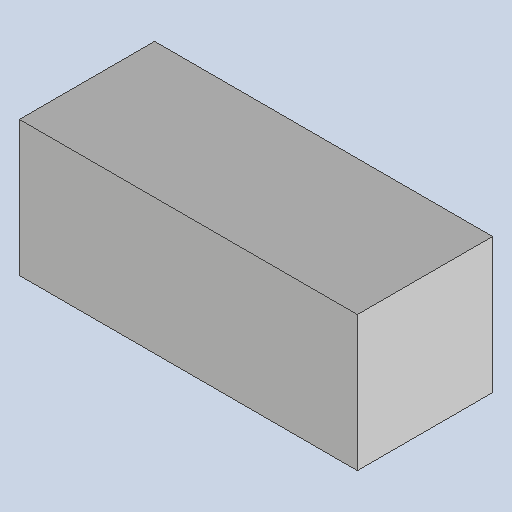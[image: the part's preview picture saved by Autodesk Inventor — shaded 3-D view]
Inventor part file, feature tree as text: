
AUTODESK INVENTOR PART (.ipt)
format: ipt  version: 2025 (Build 290162010, 162A)  size: 140,288 bytes
history: native  units: mm
features: extrude x1, sketch x1
ambient origin geometry x8: Origin, YZ Plane, XZ Plane, XY Plane, X Axis, Y Axis, Z Axis, Center Point
bodies: Volumenkörper1 (feature_tree)
feature tree (2):
  extrude  "Extrusion1"  Depth=0.2mm
  sketch  "Skizze1"  dims[d1=0.5mm d2=0.0mm d3=0.2mm d4=0.2mm]
